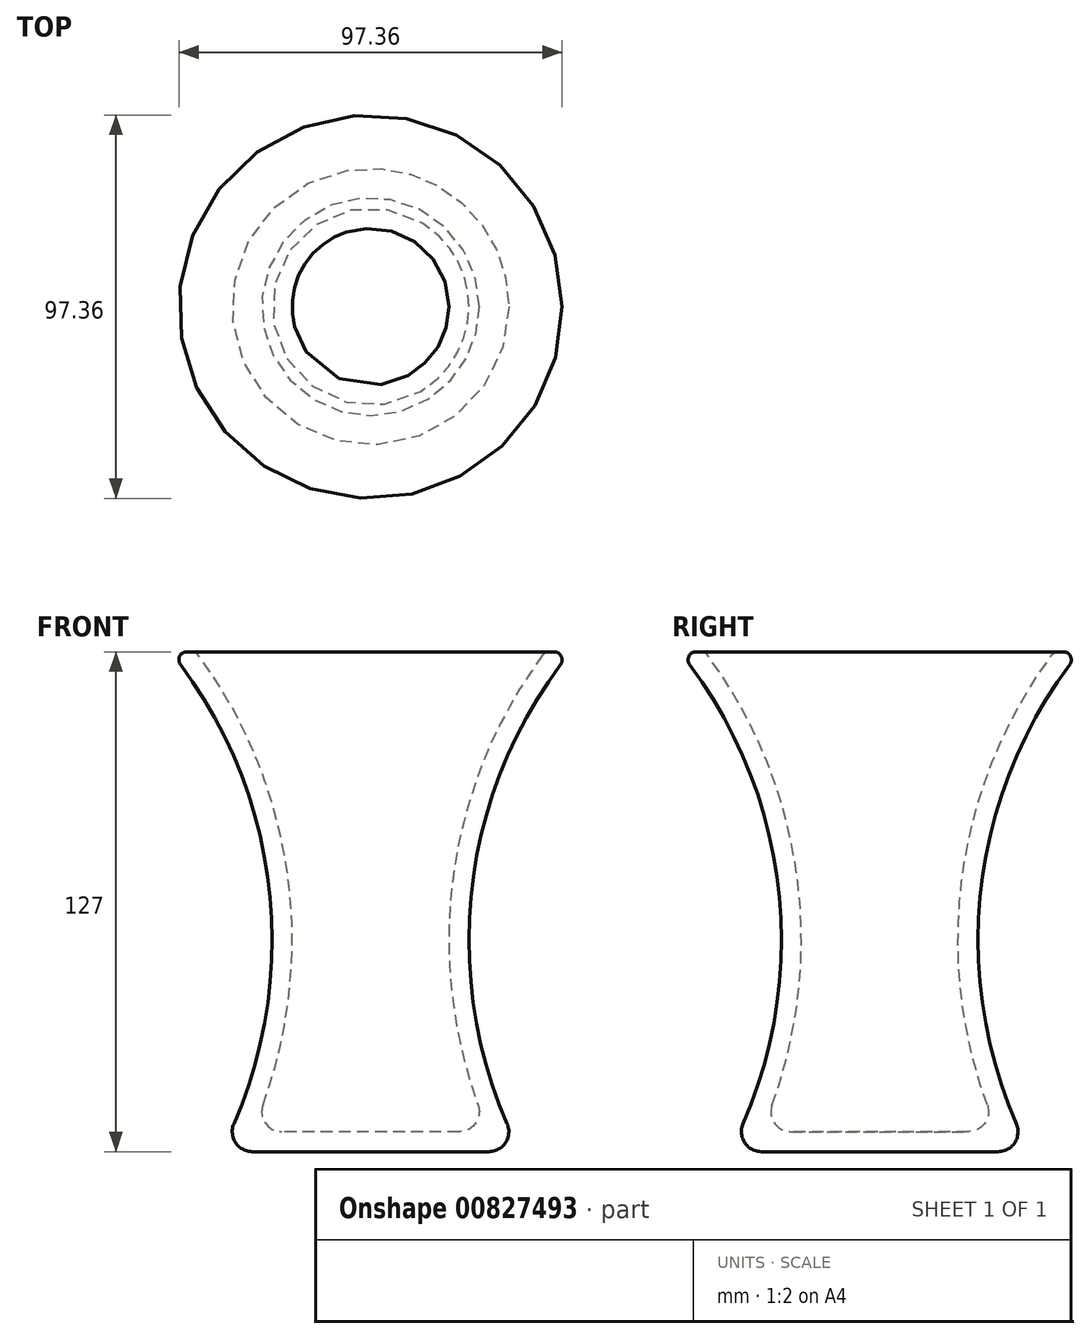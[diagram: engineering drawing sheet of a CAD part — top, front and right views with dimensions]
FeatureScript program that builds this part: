
annotation { "Feature Type Name" : "Feature", "Feature Type Description" : "" }
export const myFeature = defineFeature(function(context is Context, id is Id, definition is map)
    precondition{}
    {
        {
            var Q0;
            Q0=qCreatedBy(makeId("Front.planeOp"),FACE);
            var sketch = newSketch(context, id + "F0", { "sketchPlane" : qUnion([Q0])});
            skLineSegment(sketch, "E0", {"start": v(-7.28, 71.02) * mm, "end": v(-7.28, -55.98) * mm});
            skLineSegment(sketch, "E1", {"start": v(-7.28, 71.02) * mm, "end": v(-58.08, 71.02) * mm});
            skLineSegment(sketch, "E2", {"start": v(-7.28, -55.98) * mm, "end": v(-45.38, -55.98) * mm});
            skArc(sketch, "E3", {"start": v(-45.38, -55.98) * mm, "mid": v(-32.85, 9.4) * mm, "end": v(-58.08, 71.02) * mm});
            skSolve(sketch);
        }
        {
            var Q0;
            Q0=makeQuery(id+"F0.imprint","IMPRINT",FACE,{"disambiguationData":[TD([[makeQuery(id+"F0.imprint","IMPRINT",EDGE,{"derivedFrom":sQuery(id+"F0.wireOp",EDGE,"E0")}),-1.0]])]});
            var Q1;
            Q1=sQuery(id+"F0.wireOp",EDGE,"E0");
            revolve(context, id + "F1", {"surfaceOperationType" : NewSurfaceOperationType.NEW, "entities" : qUnion([Q0]), "axis" : qUnion([Q1]), "revolveType" : RevolveType.FULL});
        }
        {
            var Q0;
            Q0=makeQuery(id+"F1.opRevolve","SWEPT_FACE",FACE,{"disambiguationData":[OSD([sQuery(id+"F0.wireOp",EDGE,"E1")])]});
            shell(context, id + "F2", {"entities" : qUnion([Q0]), "thickness" : 5.08 * mm});
        }
        {
            var Q0;
            Q0=makeQuery(id+"F2.opShell","OFFSET_EDGE",EDGE,{"disambiguationData":[OSD([sQuery(id+"F0.wireOp",EDGE,"E1"),sQuery(id+"F0.wireOp",EDGE,"E3")])]});
            var Q1;
            Q1=makeQuery(id+"F1.opRevolve","SWEPT_EDGE",EDGE,{"disambiguationData":[OSD([sQuery(id+"F0.wireOp",EDGE,"E1"),sQuery(id+"F0.wireOp",EDGE,"E3")])]});
            fillet(context, id + "F3", {"entities" : qUnion([Q0, Q1]), "radius" : 2.03 * mm, "tangentPropagation" : true, "allowEdgeOverflow" : false});
        }
        {
            var Q0;
            Q0=makeQuery(id+"F2.opShell","OFFSET_FACE",FACE,{"disambiguationData":[OSD([sQuery(id+"F0.wireOp",EDGE,"E3")])]});
            fillet(context, id + "F4", {"entities" : qUnion([Q0]), "radius" : 5.08 * mm, "tangentPropagation" : true, "allowEdgeOverflow" : false});
        }
        {
            var Q0;
            Q0=makeQuery(id+"F1.opRevolve","SWEPT_EDGE",EDGE,{"disambiguationData":[OSD([sQuery(id+"F0.wireOp",EDGE,"E2"),sQuery(id+"F0.wireOp",EDGE,"E3")])]});
            fillet(context, id + "F5", {"entities" : qUnion([Q0]), "radius" : 5.08 * mm, "tangentPropagation" : true, "allowEdgeOverflow" : false});
        }
    });
